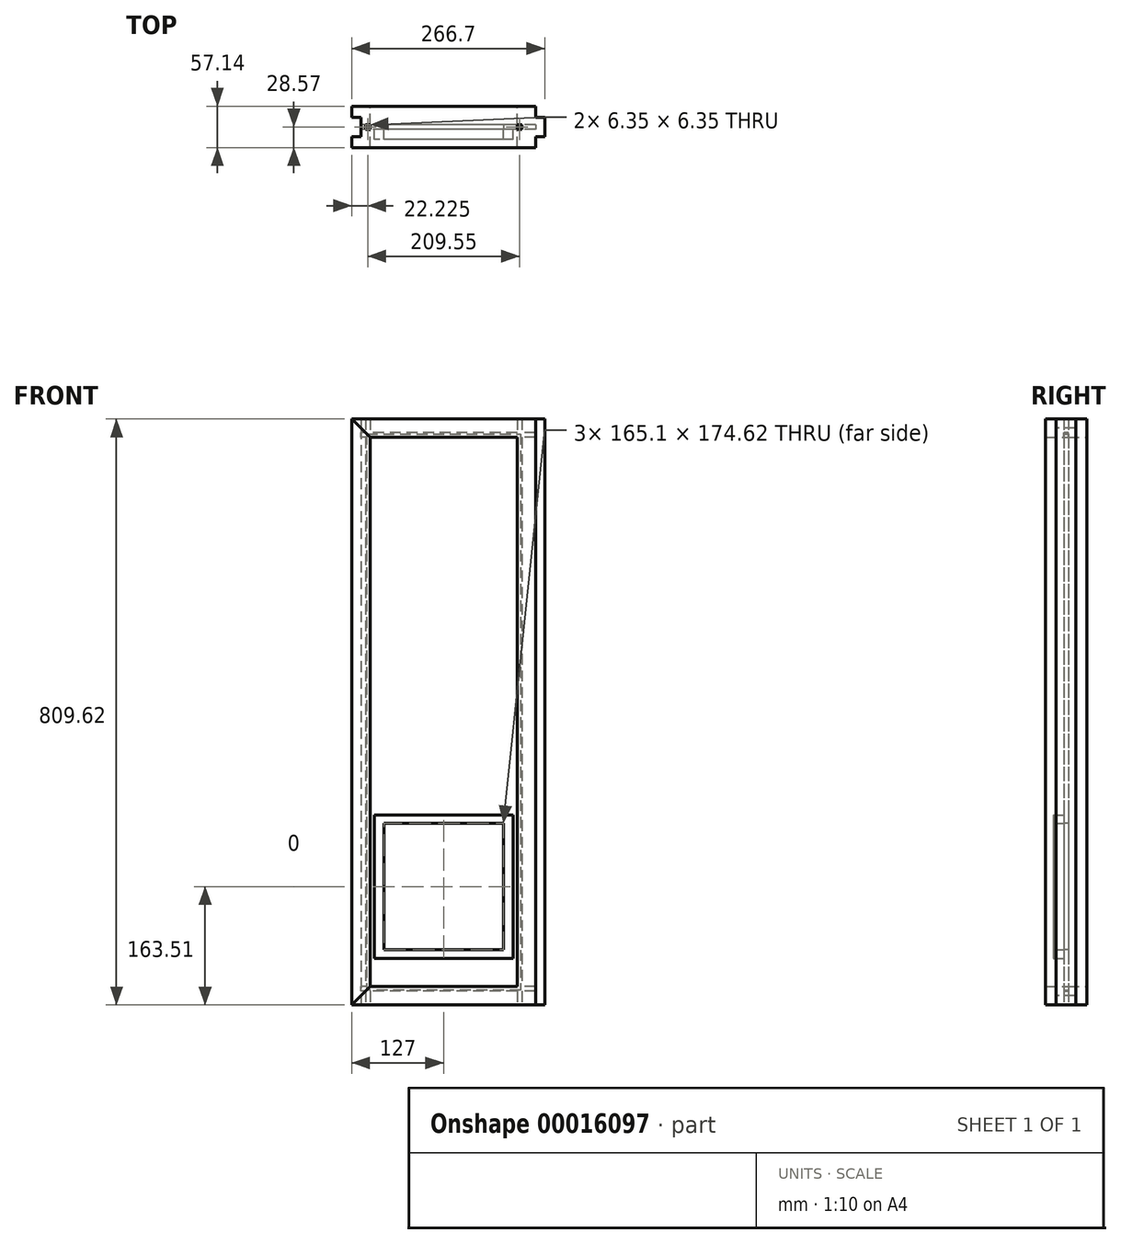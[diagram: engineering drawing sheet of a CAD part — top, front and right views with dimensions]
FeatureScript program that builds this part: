
annotation { "Feature Type Name" : "Feature", "Feature Type Description" : "" }
export const myFeature = defineFeature(function(context is Context, id is Id, definition is map)
    precondition{}
    {
        {
            var Q0;
            Q0=qCreatedBy(makeId("Front.planeOp"),FACE);
            var sketch = newSketch(context, id + "F0", { "sketchPlane" : qUnion([Q0])});
            skLineSegment(sketch, "E0.rect.bottom", {"start": v(127, 404.81) * mm, "end": v(-127, 404.81) * mm});
            skLineSegment(sketch, "E0.rect.top", {"start": v(127, -404.81) * mm, "end": v(-127, -404.81) * mm});
            skLineSegment(sketch, "E0.rect.left", {"start": v(127, 404.81) * mm, "end": v(127, -404.81) * mm});
            skLineSegment(sketch, "E0.rect.right", {"start": v(-127, 404.81) * mm, "end": v(-127, -404.81) * mm});
            skPoint(sketch, "E0.rect.middle", {"position": v(0, 0) * mm});
            skLineSegment(sketch, "E1.0", {"start": v(101.6, 379.41) * mm, "end": v(-101.6, 379.41) * mm});
            skLineSegment(sketch, "E1.1", {"start": v(101.6, 379.41) * mm, "end": v(101.6, -379.41) * mm});
            skLineSegment(sketch, "E1.2", {"start": v(101.6, -379.41) * mm, "end": v(-101.6, -379.41) * mm});
            skLineSegment(sketch, "E1.3", {"start": v(-101.6, 379.41) * mm, "end": v(-101.6, -379.41) * mm});
            skLineSegment(sketch, "E2", {"start": v(-127, 404.81) * mm, "end": v(-101.6, 379.41) * mm});
            skLineSegment(sketch, "E3", {"start": v(101.6, 379.41) * mm, "end": v(127, 404.81) * mm});
            skLineSegment(sketch, "E4", {"start": v(127, -404.81) * mm, "end": v(101.6, -379.41) * mm});
            skLineSegment(sketch, "E5", {"start": v(-127, -404.81) * mm, "end": v(-101.6, -379.41) * mm});
            skSolve(sketch);
        }
        {
            var Q0;
            Q0=makeQuery(id+"F0.imprint","IMPRINT",FACE,{"disambiguationData":[TD([[makeQuery(id+"F0.imprint","IMPRINT",EDGE,{"derivedFrom":sQuery(id+"F0.wireOp",EDGE,"E0.rect.right")}),1.0]])]});
            extrude(context, id + "F1", {"entities" : qUnion([Q0]), "endBound" : BoundingType.SYMMETRIC, "depth" : 57.15 * mm});
        }
        {
            var Q0;
            Q0=makeQuery(id+"F0.imprint","IMPRINT",FACE,{"disambiguationData":[TD([[makeQuery(id+"F0.imprint","IMPRINT",EDGE,{"derivedFrom":sQuery(id+"F0.wireOp",EDGE,"E0.rect.bottom")}),1.0]])]});
            var Q1;
            Q1=makeQuery(id+"F1.opExtrude","CAP_FACE",FACE,{"disambiguationData":[OSD([sQuery(id+"F0.wireOp",EDGE,"E0.rect.right"),sQuery(id+"F0.wireOp",EDGE,"E1.3"),sQuery(id+"F0.wireOp",EDGE,"E2"),sQuery(id+"F0.wireOp",EDGE,"E5")])],"isStart":false});
            var Q2;
            Q2=makeQuery(id+"F1.opExtrude","CAP_FACE",FACE,{"disambiguationData":[OSD([sQuery(id+"F0.wireOp",EDGE,"E0.rect.right"),sQuery(id+"F0.wireOp",EDGE,"E1.3"),sQuery(id+"F0.wireOp",EDGE,"E2"),sQuery(id+"F0.wireOp",EDGE,"E5")])],"isStart":true});
            extrude(context, id + "F2", {"entities" : qUnion([Q0]), "endBound" : BoundingType.UP_TO_SURFACE, "endBoundEntityFace" : qUnion([Q1]), "depth" : 25.4 * mm, "hasSecondDirection" : true, "secondDirectionBound" : SecondDirectionBoundingType.UP_TO_SURFACE, "secondDirectionOppositeDirection" : true, "secondDirectionBoundEntityFace" : qUnion([Q2]), "secondDirectionDepth" : 25.4 * mm});
        }
        {
            var Q0;
            Q0=makeQuery(id+"F0.imprint","IMPRINT",FACE,{"disambiguationData":[TD([[makeQuery(id+"F0.imprint","IMPRINT",EDGE,{"derivedFrom":sQuery(id+"F0.wireOp",EDGE,"E0.rect.left")}),-1.0]])]});
            var Q1;
            Q1=makeQuery(id+"F1.opExtrude","CAP_FACE",FACE,{"disambiguationData":[OSD([sQuery(id+"F0.wireOp",EDGE,"E0.rect.right"),sQuery(id+"F0.wireOp",EDGE,"E1.3"),sQuery(id+"F0.wireOp",EDGE,"E2"),sQuery(id+"F0.wireOp",EDGE,"E5")])],"isStart":false});
            var Q2;
            Q2=makeQuery(id+"F2.opExtrude","CAP_FACE",FACE,{"disambiguationData":[OSD([sQuery(id+"F0.wireOp",EDGE,"E0.rect.bottom"),sQuery(id+"F0.wireOp",EDGE,"E1.0"),sQuery(id+"F0.wireOp",EDGE,"E2"),sQuery(id+"F0.wireOp",EDGE,"E3")])],"isStart":true});
            extrude(context, id + "F3", {"entities" : qUnion([Q0]), "endBound" : BoundingType.UP_TO_SURFACE, "endBoundEntityFace" : qUnion([Q1]), "depth" : 25.4 * mm, "hasSecondDirection" : true, "secondDirectionBound" : SecondDirectionBoundingType.UP_TO_SURFACE, "secondDirectionOppositeDirection" : true, "secondDirectionBoundEntityFace" : qUnion([Q2]), "secondDirectionDepth" : 25.4 * mm});
        }
        {
            var Q0;
            Q0=makeQuery(id+"F0.imprint","IMPRINT",FACE,{"disambiguationData":[TD([[makeQuery(id+"F0.imprint","IMPRINT",EDGE,{"derivedFrom":sQuery(id+"F0.wireOp",EDGE,"E0.rect.top")}),-1.0]])]});
            var Q1;
            Q1=makeQuery(id+"F1.opExtrude","CAP_FACE",FACE,{"disambiguationData":[OSD([sQuery(id+"F0.wireOp",EDGE,"E0.rect.right"),sQuery(id+"F0.wireOp",EDGE,"E1.3"),sQuery(id+"F0.wireOp",EDGE,"E2"),sQuery(id+"F0.wireOp",EDGE,"E5")])],"isStart":false});
            var Q2;
            Q2=makeQuery(id+"F1.opExtrude","CAP_FACE",FACE,{"disambiguationData":[OSD([sQuery(id+"F0.wireOp",EDGE,"E0.rect.right"),sQuery(id+"F0.wireOp",EDGE,"E1.3"),sQuery(id+"F0.wireOp",EDGE,"E2"),sQuery(id+"F0.wireOp",EDGE,"E5")])],"isStart":true});
            extrude(context, id + "F4", {"entities" : qUnion([Q0]), "endBound" : BoundingType.UP_TO_SURFACE, "endBoundEntityFace" : qUnion([Q1]), "depth" : 25.4 * mm, "hasSecondDirection" : true, "secondDirectionBound" : SecondDirectionBoundingType.UP_TO_SURFACE, "secondDirectionOppositeDirection" : true, "secondDirectionBoundEntityFace" : qUnion([Q2]), "secondDirectionDepth" : 25.4 * mm});
        }
        {
            var Q0;
            Q0=makeQuery(id+"F4.opExtrude","SWEPT_FACE",FACE,{"disambiguationData":[OSD([sQuery(id+"F0.wireOp",EDGE,"E0.rect.top")])]});
            var sketch = newSketch(context, id + "F5", { "sketchPlane" : qUnion([Q0])});
            skLineSegment(sketch, "E6.bottom", {"start": v(-107.95, 3.17) * mm, "end": v(-101.6, 3.17) * mm});
            skLineSegment(sketch, "E6.top", {"start": v(-107.95, -3.18) * mm, "end": v(-101.6, -3.18) * mm});
            skLineSegment(sketch, "E6.left", {"start": v(-107.95, 3.18) * mm, "end": v(-107.95, -3.18) * mm});
            skLineSegment(sketch, "E6.right", {"start": v(-101.6, 3.18) * mm, "end": v(-101.6, -3.18) * mm});
            skLineSegment(sketch, "E7", {"start": v(-107.95, 0) * mm, "end": v(-127, 0) * mm, "construction": true});
            skLineSegment(sketch, "E8", {"start": v(0, 28.58) * mm, "end": v(0, -28.58) * mm, "construction": true});
            skLineSegment(sketch, "E9.MirrorCS", {"start": v(107.95, 3.18) * mm, "end": v(107.95, -3.17) * mm});
            skLineSegment(sketch, "E10.MirrorCS", {"start": v(107.95, -3.17) * mm, "end": v(101.6, -3.17) * mm});
            skLineSegment(sketch, "E11.MirrorCS", {"start": v(107.95, 3.18) * mm, "end": v(101.6, 3.18) * mm});
            skLineSegment(sketch, "E12.MirrorCS", {"start": v(101.6, 3.18) * mm, "end": v(101.6, -3.18) * mm});
            skLineSegment(sketch, "E13.MirrorCS", {"start": v(101.6, 3.18) * mm, "end": v(101.6, -3.17) * mm});
            skSolve(sketch);
        }
        {
            var Q0;
            Q0 = qSketchRegion(id + "F5", true);
            extrude(context, id + "F6", {"entities" : qUnion([Q0]), "operationType" : NewBodyOperationType.REMOVE, "endBound" : BoundingType.THROUGH_ALL, "oppositeDirection" : true, "depth" : 25.4 * mm});
        }
        {
            var Q0;
            Q0=makeQuery(id+"F1.opExtrude","SWEPT_FACE",FACE,{"disambiguationData":[OSD([sQuery(id+"F0.wireOp",EDGE,"E0.rect.right")])]});
            var sketch = newSketch(context, id + "F7", { "sketchPlane" : qUnion([Q0])});
            skLineSegment(sketch, "E14.bottom", {"start": v(3.18, 385.76) * mm, "end": v(-3.18, 385.76) * mm});
            skLineSegment(sketch, "E14.top", {"start": v(3.18, 379.41) * mm, "end": v(-3.18, 379.41) * mm});
            skLineSegment(sketch, "E14.left", {"start": v(3.17, 385.76) * mm, "end": v(3.17, 379.41) * mm});
            skLineSegment(sketch, "E14.right", {"start": v(-3.18, 385.76) * mm, "end": v(-3.18, 379.41) * mm});
            skLineSegment(sketch, "E15", {"start": v(0, 385.76) * mm, "end": v(0, 404.81) * mm, "construction": true});
            skLineSegment(sketch, "E16", {"start": v(28.58, 0) * mm, "end": v(-28.58, 0) * mm, "construction": true});
            skLineSegment(sketch, "E17.MirrorCS", {"start": v(3.18, -385.76) * mm, "end": v(-3.18, -385.76) * mm});
            skLineSegment(sketch, "E18.MirrorCS", {"start": v(3.18, -379.41) * mm, "end": v(-3.18, -379.41) * mm});
            skLineSegment(sketch, "E19.MirrorCS", {"start": v(3.17, -385.76) * mm, "end": v(3.17, -379.41) * mm});
            skLineSegment(sketch, "E20.MirrorCS", {"start": v(-3.18, -385.76) * mm, "end": v(-3.18, -379.41) * mm});
            skSolve(sketch);
        }
        {
            var Q0;
            Q0 = qSketchRegion(id + "F7", true);
            extrude(context, id + "F8", {"entities" : qUnion([Q0]), "operationType" : NewBodyOperationType.REMOVE, "endBound" : BoundingType.THROUGH_ALL, "oppositeDirection" : true, "depth" : 25.4 * mm});
        }
        {
            var Q0;
            Q0=makeQuery(id+"F4.opExtrude","SWEPT_FACE",FACE,{"disambiguationData":[OSD([sQuery(id+"F0.wireOp",EDGE,"E0.rect.top")])]});
            var sketch = newSketch(context, id + "F9", { "sketchPlane" : qUnion([Q0])});
            skLineSegment(sketch, "E21.bottom", {"start": v(-127, 13.5) * mm, "end": v(-114.3, 13.5) * mm});
            skLineSegment(sketch, "E21.top", {"start": v(-127, -13.5) * mm, "end": v(-114.3, -13.5) * mm});
            skLineSegment(sketch, "E21.left", {"start": v(-127, 13.5) * mm, "end": v(-127, -13.5) * mm});
            skLineSegment(sketch, "E21.right", {"start": v(-114.3, 13.5) * mm, "end": v(-114.3, -13.5) * mm});
            skLineSegment(sketch, "E22", {"start": v(-114.3, 0) * mm, "end": v(0, 0) * mm, "construction": true});
            skLineSegment(sketch, "E23.bottom", {"start": v(139.7, 13.5) * mm, "end": v(127, 13.5) * mm});
            skLineSegment(sketch, "E23.top", {"start": v(139.7, -13.5) * mm, "end": v(127, -13.5) * mm});
            skLineSegment(sketch, "E23.left", {"start": v(127, 13.5) * mm, "end": v(127, -13.5) * mm});
            skLineSegment(sketch, "E23.right", {"start": v(139.7, 13.5) * mm, "end": v(139.7, -13.5) * mm});
            skSolve(sketch);
        }
        {
            var Q0;
            Q0=makeQuery(id+"F9.imprint","IMPRINT",FACE,{"disambiguationData":[TD([[makeQuery(id+"F9.imprint","IMPRINT",EDGE,{"derivedFrom":sQuery(id+"F9.wireOp",EDGE,"E21.bottom")}),-1.0]])]});
            extrude(context, id + "F10", {"entities" : qUnion([Q0]), "operationType" : NewBodyOperationType.REMOVE, "endBound" : BoundingType.THROUGH_ALL, "oppositeDirection" : true, "depth" : 25.4 * mm});
        }
        {
            var Q0;
            Q0=makeQuery(id+"F9.imprint","IMPRINT",FACE,{"disambiguationData":[TD([[makeQuery(id+"F9.imprint","IMPRINT",EDGE,{"derivedFrom":sQuery(id+"F9.wireOp",EDGE,"E23.bottom")}),1.0]])]});
            var Q1;
            Q1=makeQuery(id+"F2.opExtrude","SWEPT_FACE",FACE,{"disambiguationData":[OSD([sQuery(id+"F0.wireOp",EDGE,"E0.rect.bottom")])]});
            extrude(context, id + "F11", {"entities" : qUnion([Q0]), "operationType" : NewBodyOperationType.ADD, "endBound" : BoundingType.UP_TO_SURFACE, "oppositeDirection" : true, "endBoundEntityFace" : qUnion([Q1]), "depth" : 25.4 * mm});
        }
        {
            var Q0;
            Q0=qCreatedBy(makeId("Front.planeOp"),FACE);
            var sketch = newSketch(context, id + "F12", { "sketchPlane" : qUnion([Q0])});
            skLineSegment(sketch, "E24.0.1", {"start": v(-107.95, 385.76) * mm, "end": v(-107.95, -385.76) * mm, "construction": true});
            skLineSegment(sketch, "E24.0.3", {"start": v(-107.95, -385.76) * mm, "end": v(-107.95, 385.76) * mm, "construction": true});
            skLineSegment(sketch, "E25.0.0", {"start": v(107.95, 385.76) * mm, "end": v(107.95, -385.76) * mm, "construction": true});
            skLineSegment(sketch, "E25.0.2", {"start": v(107.95, -385.76) * mm, "end": v(107.95, 385.76) * mm, "construction": true});
            skLineSegment(sketch, "E26.0.1", {"start": v(107.95, -385.76) * mm, "end": v(-107.95, -385.76) * mm, "construction": true});
            skLineSegment(sketch, "E26.0.3", {"start": v(-107.95, -385.76) * mm, "end": v(107.95, -385.76) * mm, "construction": true});
            skLineSegment(sketch, "E27.0.0", {"start": v(-107.95, 385.76) * mm, "end": v(107.95, 385.76) * mm, "construction": true});
            skLineSegment(sketch, "E27.0.2", {"start": v(107.95, 385.76) * mm, "end": v(-107.95, 385.76) * mm, "construction": true});
            skLineSegment(sketch, "E28.0", {"start": v(106.36, 384.17) * mm, "end": v(106.36, -384.18) * mm});
            skLineSegment(sketch, "E28.1", {"start": v(-106.36, 384.18) * mm, "end": v(106.36, 384.17) * mm});
            skLineSegment(sketch, "E28.2", {"start": v(-106.36, 384.18) * mm, "end": v(-106.36, -384.17) * mm});
            skLineSegment(sketch, "E28.3", {"start": v(106.36, -384.18) * mm, "end": v(-106.36, -384.18) * mm});
            skSolve(sketch);
        }
        {
            var Q0;
            Q0 = qSketchRegion(id + "F12", true);
            extrude(context, id + "F13", {"entities" : qUnion([Q0]), "depth" : 3.17 * mm, "hasSecondDirection" : true, "secondDirectionOppositeDirection" : true, "secondDirectionDepth" : 3.17 * mm});
        }
        {
            var Q0;
            Q0=makeQuery(id+"F13.opExtrude","CAP_FACE",FACE,{"disambiguationData":[OSD([sQuery(id+"F12.wireOp",EDGE,"E28.0"),sQuery(id+"F12.wireOp",EDGE,"E28.1"),sQuery(id+"F12.wireOp",EDGE,"E28.2"),sQuery(id+"F12.wireOp",EDGE,"E28.3")])],"isStart":false});
            var sketch = newSketch(context, id + "F14", { "sketchPlane" : qUnion([Q0])});
            skLineSegment(sketch, "E29.rect.bottom", {"start": v(82.55, -153.99) * mm, "end": v(-82.55, -153.99) * mm});
            skLineSegment(sketch, "E29.rect.top", {"start": v(82.55, -328.61) * mm, "end": v(-82.55, -328.61) * mm});
            skLineSegment(sketch, "E29.rect.left", {"start": v(82.55, -153.99) * mm, "end": v(82.55, -328.61) * mm});
            skLineSegment(sketch, "E29.rect.right", {"start": v(-82.55, -153.99) * mm, "end": v(-82.55, -328.61) * mm});
            skPoint(sketch, "E29.rect.middle", {"position": v(0, -241.3) * mm});
            skSolve(sketch);
        }
        {
            var Q0;
            Q0 = qSketchRegion(id + "F14", true);
            extrude(context, id + "F15", {"entities" : qUnion([Q0]), "operationType" : NewBodyOperationType.REMOVE, "endBound" : BoundingType.THROUGH_ALL, "oppositeDirection" : true, "depth" : 25.4 * mm});
        }
        {
            var Q0;
            Q0=makeQuery(id+"F13.opExtrude","CAP_FACE",FACE,{"disambiguationData":[OSD([sQuery(id+"F12.wireOp",EDGE,"E28.0"),sQuery(id+"F12.wireOp",EDGE,"E28.1"),sQuery(id+"F12.wireOp",EDGE,"E28.2"),sQuery(id+"F12.wireOp",EDGE,"E28.3")])],"isStart":false});
            var sketch = newSketch(context, id + "F16", { "sketchPlane" : qUnion([Q0])});
            skLineSegment(sketch, "E30", {"start": v(0, -153.99) * mm, "end": v(0, -328.61) * mm, "construction": true});
            skLineSegment(sketch, "E31.rect.bottom", {"start": v(96.04, -142.08) * mm, "end": v(-96.04, -142.08) * mm});
            skLineSegment(sketch, "E31.rect.top", {"start": v(96.04, -340.52) * mm, "end": v(-96.04, -340.52) * mm});
            skLineSegment(sketch, "E31.rect.left", {"start": v(96.04, -142.08) * mm, "end": v(96.04, -340.52) * mm});
            skLineSegment(sketch, "E31.rect.right", {"start": v(-96.04, -142.08) * mm, "end": v(-96.04, -340.52) * mm});
            skPoint(sketch, "E31.rect.middle", {"position": v(0, -241.3) * mm});
            skSolve(sketch);
        }
        {
            var Q0;
            Q0=makeQuery(id+"F16.imprint","IMPRINT",FACE,{"disambiguationData":[TD([[makeQuery(id+"F16.imprint","IMPRINT",EDGE,{"derivedFrom":sQuery(id+"F16.wireOp",EDGE,"E31.rect.bottom")}),1.0]])]});
            extrude(context, id + "F17", {"entities" : qUnion([Q0]), "depth" : 14.29 * mm});
        }
        {
            var Q0;
            Q0=makeQuery(id+"F13.opExtrude","CAP_FACE",FACE,{"disambiguationData":[OSD([sQuery(id+"F12.wireOp",EDGE,"E28.0"),sQuery(id+"F12.wireOp",EDGE,"E28.1"),sQuery(id+"F12.wireOp",EDGE,"E28.2"),sQuery(id+"F12.wireOp",EDGE,"E28.3")])],"isStart":true});
            var sketch = newSketch(context, id + "F18", { "sketchPlane" : qUnion([Q0])});
            skLineSegment(sketch, "E32.0", {"start": v(-96.04, -142.08) * mm, "end": v(96.04, -142.08) * mm});
            skLineSegment(sketch, "E32.1", {"start": v(-96.04, -142.08) * mm, "end": v(-96.04, -340.52) * mm});
            skLineSegment(sketch, "E32.2", {"start": v(96.04, -142.08) * mm, "end": v(96.04, -340.52) * mm});
            skLineSegment(sketch, "E32.3", {"start": v(-96.04, -340.52) * mm, "end": v(96.04, -340.52) * mm});
            skSolve(sketch);
        }
        {
            var Q0;
            Q0=makeQuery(id+"F18.imprint","IMPRINT",FACE,{"disambiguationData":[TD([[makeQuery(id+"F18.imprint","IMPRINT",EDGE,{"derivedFrom":sQuery(id+"F18.wireOp",EDGE,"E32.0")}),-1.0]])]});
            extrude(context, id + "F19", {"entities" : qUnion([Q0]), "depth" : 3 / 203.2 * mm});
        }
    });
